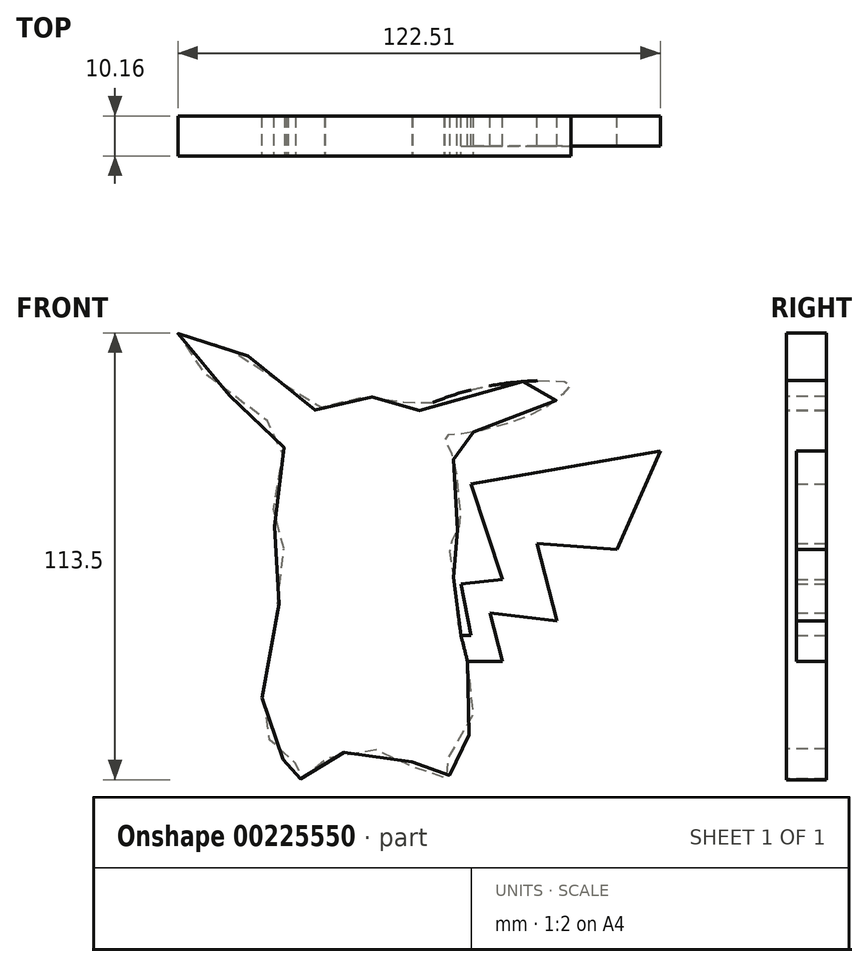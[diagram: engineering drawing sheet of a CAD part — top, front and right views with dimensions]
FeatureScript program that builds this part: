
annotation { "Feature Type Name" : "Feature", "Feature Type Description" : "" }
export const myFeature = defineFeature(function(context is Context, id is Id, definition is map)
    precondition{}
    {
        {
            var Q0;
            Q0=qCreatedBy(makeId("Front.planeOp"),FACE);
            var sketch = newSketch(context, id + "F0", { "sketchPlane" : qUnion([Q0])});
            skFitSpline(sketch, "E0", {"points": [v(-16.52, 39.79) * mm, v(-14.62, 40.23) * mm, v(-9.35, 42.25) * mm, v(-1.96, 43.15) * mm, v(2.3, 42.59) * mm, v(7.67, 41.47) * mm, v(10.8, 39.56) * mm, v(11.48, 40) * mm, v(29.06, 45.95) * mm, v(49.45, 46.62) * mm, v(49.23, 45.95) * mm, v(45.64, 42.14) * mm, v(34.78, 36.76) * mm, v(21.9, 33.74) * mm, v(17.86, 33.29) * mm, v(17.42, 32.73) * mm, v(19.54, 27.58) * mm, v(21, 16.49) * mm, v(21.22, 10.55) * mm, v(18.87, 5.85) * mm, v(18.76, 2.94) * mm, v(19.32, -0.87) * mm, v(20.33, -6.7) * mm, v(20.44, -12.4) * mm, v(21.5, -17.46) * mm, v(23.8, -27.2) * mm, v(24.58, -36.27) * mm, v(22.68, -44.33) * mm, v(17.42, -49.37) * mm, v(17.42, -50.04) * mm, v(18.65, -52.28) * mm, v(17.86, -53.85) * mm, v(14.17, -53.74) * mm, v(9.13, -50.94) * mm, v(9.13, -49.7) * mm, v(1.73, -46.9) * mm, v(-5.88, -46.68) * mm, v(-13.05, -49.37) * mm, v(-13.05, -50.72) * mm, v(-17.3, -53.63) * mm, v(-22.01, -53.52) * mm, v(-22.23, -52.5) * mm, v(-20.44, -49.93) * mm, v(-22.57, -49.6) * mm, v(-26.5, -45.12) * mm, v(-28.96, -38.73) * mm, v(-28.28, -28.76) * mm, v(-25.6, -14.99) * mm, v(-23.58, 5.18) * mm, v(-25.03, 7.08) * mm, v(-26.04, 15.48) * mm, v(-24.59, 24.1) * mm, v(-22.8, 33.85) * mm, v(-23.02, 34.19) * mm, v(-37.47, 43.6) * mm, v(-47.1, 53.45) * mm, v(-50.32, 59.2) * mm, v(-49.45, 59.2) * mm, v(-39.04, 55.91) * mm, v(-27.05, 49.87) * mm, v(-16.52, 39.79) * mm]});
            skLineSegment(sketch, "E1", {"start": v(21.5, -17.46) * mm, "end": v(24.15, -17.46) * mm});
            skLineSegment(sketch, "E2", {"start": v(24.15, -17.46) * mm, "end": v(21.5, -4.46) * mm});
            skLineSegment(sketch, "E3", {"start": v(21.5, -4.46) * mm, "end": v(32.06, -3.24) * mm});
            skLineSegment(sketch, "E4", {"start": v(32.06, -3.24) * mm, "end": v(24.15, 20.97) * mm});
            skLineSegment(sketch, "E5", {"start": v(24.15, 20.97) * mm, "end": v(72.18, 29.35) * mm});
            skLineSegment(sketch, "E6", {"start": v(72.18, 29.35) * mm, "end": v(61.16, 4.3) * mm});
            skLineSegment(sketch, "E7", {"start": v(61.16, 4.3) * mm, "end": v(40.82, 5.9) * mm});
            skLineSegment(sketch, "E8", {"start": v(40.82, 5.9) * mm, "end": v(45.9, -13.79) * mm});
            skLineSegment(sketch, "E9", {"start": v(45.9, -13.79) * mm, "end": v(28.95, -11.81) * mm});
            skLineSegment(sketch, "E10", {"start": v(28.95, -11.81) * mm, "end": v(32.06, -24.15) * mm});
            skLineSegment(sketch, "E11", {"start": v(32.06, -24.15) * mm, "end": v(23.2, -24.15) * mm});
            skSolve(sketch);
        }
        {
            var Q0;
            Q0=makeQuery(id+"F0.imprint","IMPRINT",FACE,{"disambiguationData":[TD([[makeQuery(id+"F0.imprint","IMPRINT",EDGE,{"derivedFrom":sQuery(id+"F0.wireOp",EDGE,"E0")}),-1.0]])]});
            extrude(context, id + "F1", {"entities" : qUnion([Q0]), "depth" : 10.16 * mm});
        }
        {
            var Q0;
            {var subQ0=sQuery(id+"F0.wireOp",EDGE,"E1");Q0=makeQuery(id+"F0.imprint","IMPRINT",FACE,{"disambiguationData":[TD([[makeQuery(id+"F0.imprint","IMPRINT",EDGE,{"derivedFrom":subQ0}),-1.0]])]});}
            extrude(context, id + "F2", {"entities" : qUnion([Q0]), "operationType" : NewBodyOperationType.ADD, "depth" : 7.62 * mm});
        }
    });
